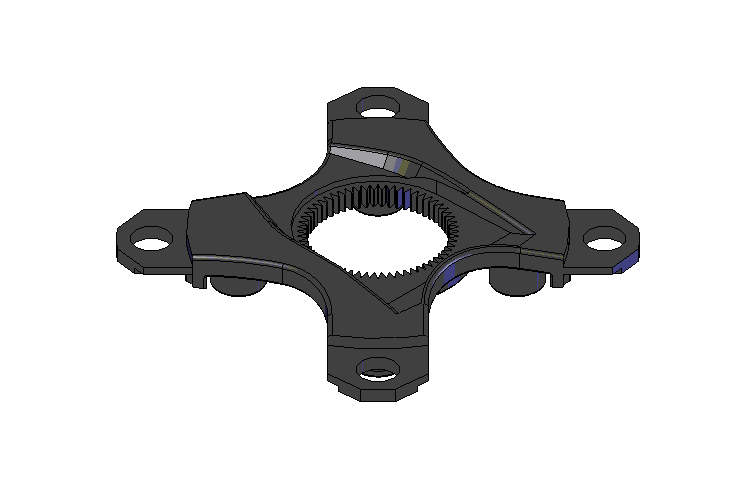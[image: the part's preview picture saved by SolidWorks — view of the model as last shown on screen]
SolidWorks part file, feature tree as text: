
SOLIDWORKS PART (.sldprt)
format: sldprt  version: not decoded by parser v0  size: 3,046,912 bytes
history: native  units: mm
features: sketch x13, cut_extrude x9, plane x5, extrude x3, fillet x2, material x1, revolve x1, pattern_circular x1 (+10 scaffold rows collapsed)
feature tree (45):
  scaffold x10  (default folders/planes/origin — collapsed)
  material  "Matériau <non spécifié>"
  plane  "Plan de face"
  plane  "Plan de dessus"
  plane  "Plan de droite"
  sketch  "Esquisse5"  dims[D2=80.0mm D1=5.5mm D3=88.0mm D4=82.0mm D5=90.0mm D6=3.5mm D7=120.0mm D8=2.0mm D9=3.0mm D10=10.0mm D11=46.0mm D12=3.0mm]
  revolve  "Révolution2"  Angle=360deg
  sketch  "Esquisse6"  dims[c1.D1=64.0mm c1.D2=13.0mm c1.D3=~58.906526mm c2.D3=90.0deg]
  extrude  "Extrusion2"  Depth=12mm
  sketch  "Esquisse7"  dims[D1=6.75mm]
  cut_extrude  "Enlèv. mat.-Extru.2"  Depth=11mm
  sketch  "Esquisse8"
  extrude  "Extrusion3"  [1 undecoded]
  sketch  "Esquisse9"  dims[D1=5.0mm]
  extrude  "Extrusion4"  [1 undecoded]
  sketch  "Esquisse10"  dims[D1=10.0mm D2=104.0mm]
  cut_extrude  "Enlèv. mat.-Extru.3"  [1 undecoded]
  sketch  "Esquisse11"  dims[c1.D1=88.0mm c1.D2=158.0mm c1.D3=88.0mm c2.D1=~38.048408mm c2.D3=45.0mm c2.D4=13.0mm c2.D6=~22.101484mm c2.D8=56.0mm c2.D9=23.0mm c2.D10=66.5mm c2.D11=18.5mm c3.D9=66.5mm c3.D10=18.5mm c3.D11=25.0mm c3.D12=18.5mm c4.D10=18.5mm c4.D12=18.5mm c4.D13=66.5mm c4.D9=18.5mm c5.D10=18.5mm c5.D11=100.0mm c5.D8=45.0mm c5.D3=~153.978222mm c5.D4=~76.989111mm c6.D3=50.0mm c6.D4=44.0mm c7.D3=~10.504153mm c7.D1=53.0mm c7.D5=58.0mm c7.D6=50.0mm c7.D7=~98.470947mm c8.D7=45.0deg c8.D12=~3.502635mm c8.D13=~2.74136mm c9.D12=58.0mm c9.D9=12.0mm c9.D10=56.0mm c9.D8=11.51mm c9.D11=2.0mm c10.D8=23.0135mm c10.D3=23.02mm c10.D2=23.0mm c11.D3=50.0mm c11.D4=8.0mm c11.D5=6.0mm]
  cut_extrude  "Enlèv. mat.-Extru.4"  [1 undecoded]
  sketch  "Esquisse12"  dims[D1=18.0mm D2=1.0mm]
  cut_extrude  "Enlèv. mat.-Extru.5"  Depth=1.5mm
  sketch  "Esquisse16"  dims[D1=33.0mm]
  cut_extrude  "Enlèv. mat.-Extru.7"  [1 undecoded]
  sketch  "Esquisse14"  dims[D1=40.0mm D2=44.0mm D3=22.0mm]
  cut_extrude  "Enlèv. mat.-Extru.6"  [1 undecoded]
  plane  "Plan2"
  plane  "Plan3"
  sketch  "Esquisse18"  dims[D1=1.5mm]
  cut_extrude  "Enlèv. mat.-Extru.9"  [1 undecoded]
  sketch  "Esquisse19"  dims[D1=30.0mm D2=30.0mm D3=40.0mm]
  cut_extrude  "Enlèv. mat.-Extru.10"  Depth=4mm
  fillet  "Congé1"  Radius=1mm
  fillet  "Congé2"  Radius=0.5mm
  sketch  "Esquisse20"  dims[c1.D1=37.0mm c1.D2=0.2mm c1.D3=~2.093104mm c2.D3=36.42deg c2.D4=~26.093815mm c3.D4=3.0deg]
  cut_extrude  "Enlèv. mat.-Extru.11"  [1 undecoded]
  pattern_circular  "Répétition circulaire1"  Count=60 Angle=6deg
decode coverage: 20 of 29 modeling features carry decoded parameters
note: ~ marks probable driven/reference dimensions
note: 8 parameter values undecoded
summary: no parameter record found for 8 features
note: suppression state not decoded; provenance and decode notes live in map.json
